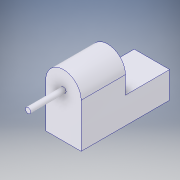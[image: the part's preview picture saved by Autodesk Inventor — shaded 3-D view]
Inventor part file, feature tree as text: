
AUTODESK INVENTOR PART (.ipt)
format: ipt  version: 2018 (Build 220112000, 112)  size: 111,616 bytes
history: native  units: in
note: dims shown in document units (in); Inventor stores cm internally (conversion verified against a paired STEP export)
features: extrude x2, sketch x2, fillet x1
ambient origin geometry x8: Origin, YZ Plane, XZ Plane, XY Plane, X Axis, Y Axis, Z Axis, Center Point
bodies: Solid1 (feature_tree)
feature tree (5):
  extrude  "Extrusion1"  Depth=0.3937in
  fillet  "Fillet1"  Radius=0.1181in
  extrude  "Extrusion2"  Depth=1.9685in
  sketch  "Sketch1"  dims[d2=0.7874in d3=0.0in d4=0.3937in d5=0.1181in]
  sketch  "Sketch3"  dims[d6=0.7874in d7=0.0in d8=1.378in d9=0.9843in d10=0.7874in d11=0.9843in d12=1.9685in]
